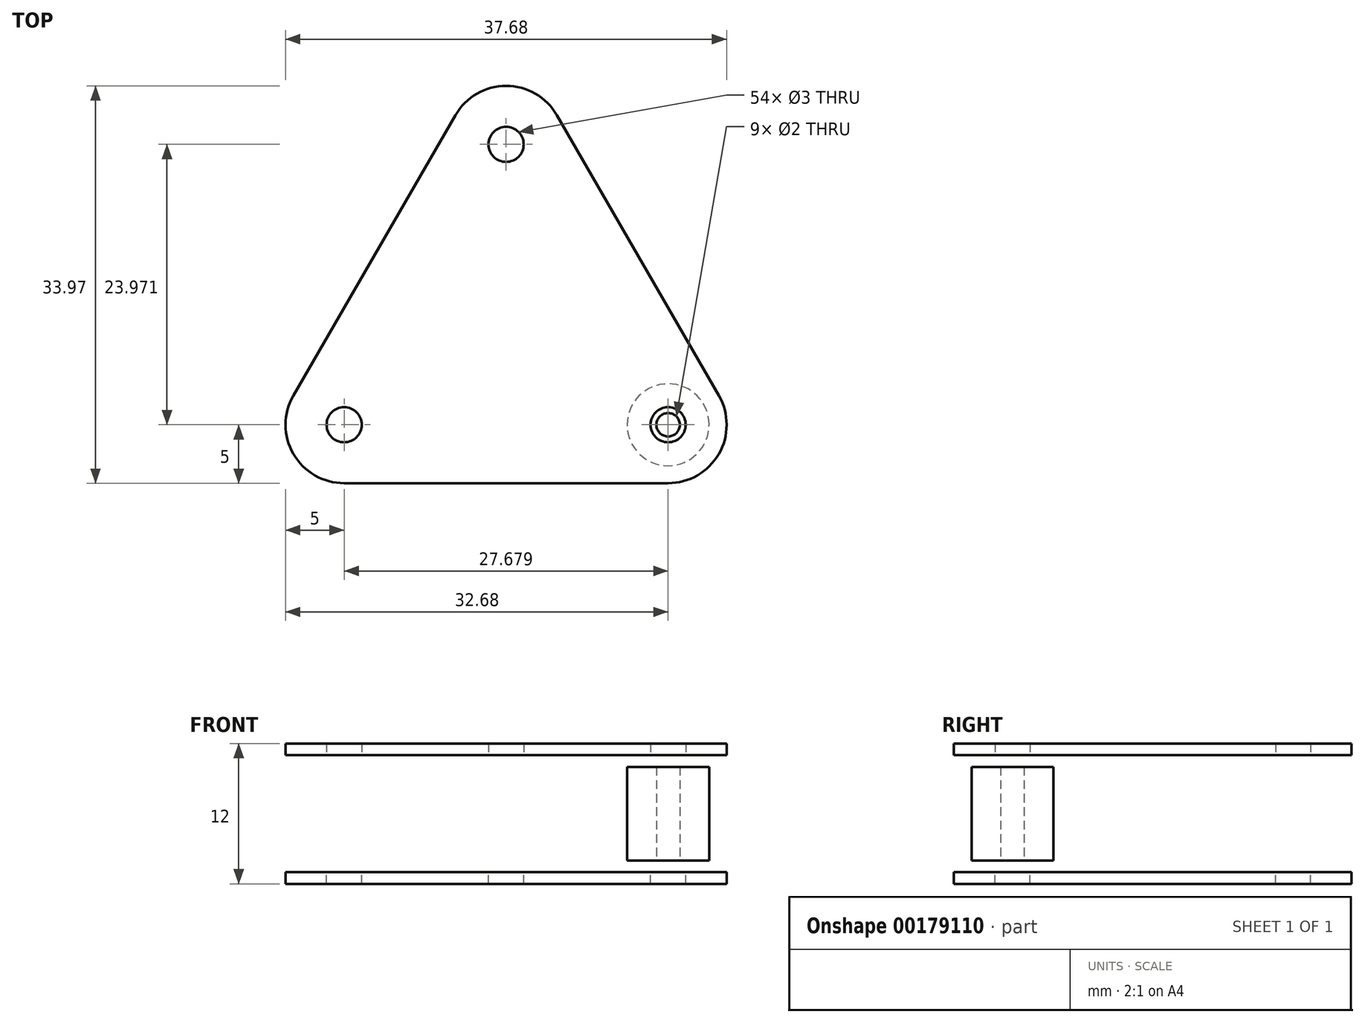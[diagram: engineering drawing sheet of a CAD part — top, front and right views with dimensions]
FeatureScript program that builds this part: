
annotation { "Feature Type Name" : "Feature", "Feature Type Description" : "" }
export const myFeature = defineFeature(function(context is Context, id is Id, definition is map)
    precondition{}
    {
        {
            var Q0;
            Q0=qCreatedBy(makeId("Top.planeOp"),FACE);
            var sketch = newSketch(context, id + "F0", { "sketchPlane" : qUnion([Q0])});
            skLineSegment(sketch, "E0", {"start": v(-4.33, 7.5) * mm, "end": v(-18.17, 31.47) * mm});
            skLineSegment(sketch, "E1", {"start": v(-26.83, 31.47) * mm, "end": v(-40.67, 7.5) * mm});
            skLineSegment(sketch, "E2", {"start": v(-36.34, 0) * mm, "end": v(-8.66, 0) * mm});
            skPoint(sketch, "E3.visualSharp", {"position": v(0, 0) * mm});
            skArc(sketch, "E3.filletArc", {"start": v(-8.66, 0) * mm, "mid": v(-4.33, 2.5) * mm, "end": v(-4.33, 7.5) * mm});
            skPoint(sketch, "E4.visualSharp", {"position": v(-22.5, 38.97) * mm});
            skArc(sketch, "E4.filletArc", {"start": v(-18.17, 31.47) * mm, "mid": v(-22.5, 33.97) * mm, "end": v(-26.83, 31.47) * mm});
            skPoint(sketch, "E5.visualSharp", {"position": v(-45, 0) * mm});
            skArc(sketch, "E5.filletArc", {"start": v(-40.67, 7.5) * mm, "mid": v(-40.67, 2.5) * mm, "end": v(-36.34, 0) * mm});
            skLineSegment(sketch, "E6.0", {"start": v(-8.66, 5) * mm, "end": v(-22.5, 28.97) * mm, "construction": true});
            skLineSegment(sketch, "E6.1", {"start": v(-36.34, 5) * mm, "end": v(-8.66, 5) * mm, "construction": true});
            skLineSegment(sketch, "E6.2", {"start": v(-22.5, 28.97) * mm, "end": v(-36.34, 5) * mm, "construction": true});
            skCircle(sketch, "E7", {"center": v(-36.34, 5) * mm, "radius": 1.5 * mm});
            skCircle(sketch, "E8", {"center": v(-22.5, 28.97) * mm, "radius": 1.5 * mm});
            skCircle(sketch, "E9", {"center": v(-8.66, 5) * mm, "radius": 1.5 * mm});
            skSolve(sketch);
        }
        {
            var Q0;
            Q0=makeQuery(id+"F0.imprint","IMPRINT",FACE,{"disambiguationData":[TD([[makeQuery(id+"F0.imprint","IMPRINT",EDGE,{"derivedFrom":sQuery(id+"F0.wireOp",EDGE,"E0")}),1.0]])]});
            extrude(context, id + "F1", {"entities" : qUnion([Q0]), "oppositeDirection" : true, "depth" : 1 * mm});
        }
        {
            var Q0;
            Q0=makeQuery(id+"F0.imprint","IMPRINT",FACE,{"disambiguationData":[TD([[makeQuery(id+"F0.imprint","IMPRINT",EDGE,{"derivedFrom":sQuery(id+"F0.wireOp",EDGE,"E0")}),1.0]])]});
            extrude(context, id + "F2", {"entities" : qUnion([Q0]), "depth" : 11 * mm, "hasSecondDirection" : true, "secondDirectionOppositeDirection" : false, "secondDirectionDepth" : 10 * mm});
        }
        {
            var Q0;
            Q0=makeQuery(id+"F0.imprint","IMPRINT",FACE,{"disambiguationData":[TD([[makeQuery(id+"F0.imprint","IMPRINT",EDGE,{"derivedFrom":sQuery(id+"F0.wireOp",EDGE,"E0")}),1.0]])]});
            var sketch = newSketch(context, id + "F3", { "sketchPlane" : qUnion([Q0])});
            skCircle(sketch, "E10", {"center": v(-8.66, 5) * mm, "radius": 1 * mm});
            skCircle(sketch, "E11", {"center": v(-8.66, 5) * mm, "radius": 3.5 * mm});
            skSolve(sketch);
        }
        {
            var Q0;
            Q0=makeQuery(id+"F3.imprint","IMPRINT",FACE,{"disambiguationData":[TD([[makeQuery(id+"F3.imprint","IMPRINT",EDGE,{"derivedFrom":sQuery(id+"F3.wireOp",EDGE,"E11")}),1.0]])]});
            var Q1;
            Q1=makeQuery(id+"F3.imprint","IMPRINT",FACE,{"disambiguationData":[TD([[makeQuery(id+"F3.imprint","IMPRINT",EDGE,{"derivedFrom":sQuery(id+"F3.wireOp",EDGE,"E10")}),-1.0]])]});
            extrude(context, id + "F4", {"entities" : qUnion([Q0, Q1]), "depth" : 9 * mm, "hasSecondDirection" : true, "secondDirectionOppositeDirection" : false, "secondDirectionDepth" : 1 * mm});
        }
    });
